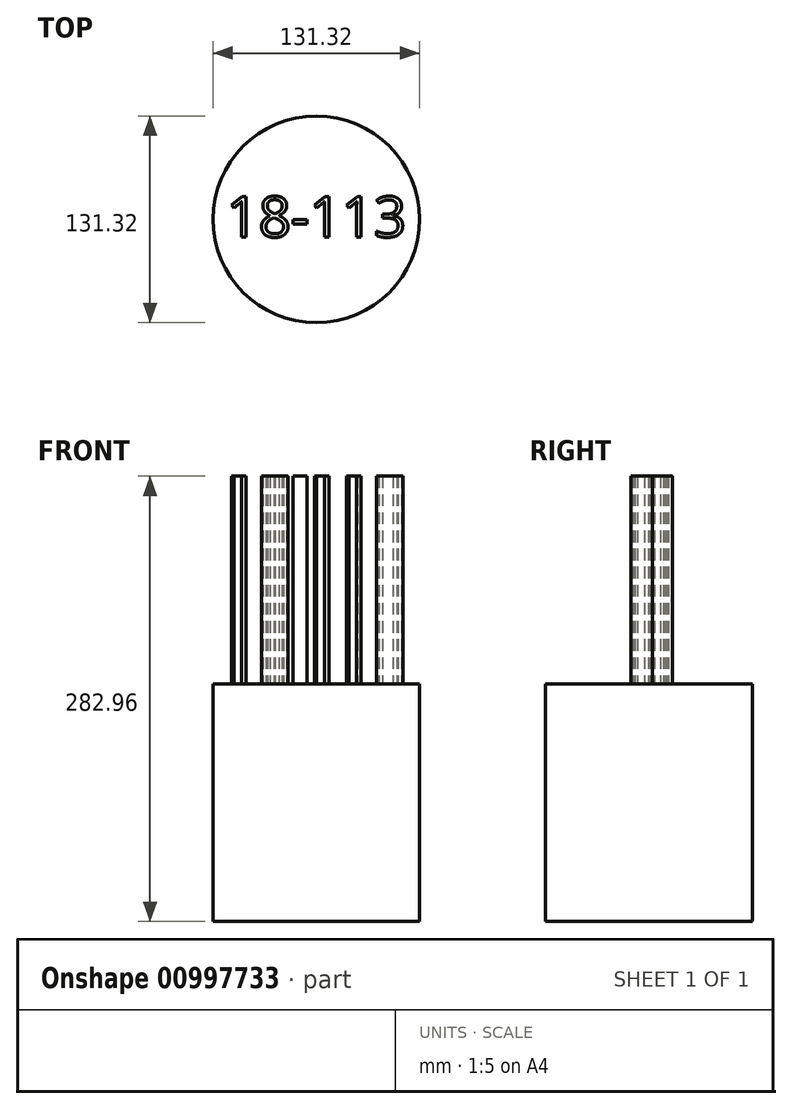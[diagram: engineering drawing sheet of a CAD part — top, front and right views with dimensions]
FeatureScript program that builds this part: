
annotation { "Feature Type Name" : "Feature", "Feature Type Description" : "" }
export const myFeature = defineFeature(function(context is Context, id is Id, definition is map)
    precondition{}
    {
        {
            var Q0;
            Q0=qCreatedBy(makeId("Top.planeOp"),FACE);
            var sketch = newSketch(context, id + "F0", { "sketchPlane" : qUnion([Q0])});
            skCircle(sketch, "E0", {"center": v(0, 0) * mm, "radius": 65.66 * mm});
            skSolve(sketch);
        }
        {
            var Q0;
            Q0 = qSketchRegion(id + "F0", true);
            extrude(context, id + "F1", {"entities" : qUnion([Q0]), "depth" : 150.88 * mm, "offsetDistance" : 25.4 * mm});
        }
        {
            var Q0;
            Q0=makeQuery(id+"F1.opExtrude","CAP_FACE",FACE,{"disambiguationData":[OSD([sQuery(id+"F0.wireOp",EDGE,"E0")])],"isStart":false});
            var sketch = newSketch(context, id + "F2", { "sketchPlane" : qUnion([Q0])});
            skText(sketch, "E1", { "text": "18-113", "fontName": "OpenSans-Regular.ttf"});
            const initialGuessF2  = {"E1": [-0.0572, -0.01124, 1, 0, 0.02585]};
            skSetInitialGuess(sketch, initialGuessF2);
            skSolve(sketch);
        }
        {
            var Q0;
            Q0=makeQuery(id+"F2.imprint","IMPRINT",FACE,{"disambiguationData":[TD([[makeQuery(id+"F2.imprint","IMPRINT",EDGE,{"derivedFrom":sQuery(id+"F2.wireOp",EDGE,"E1.sketch_text.stroke-0")}),1.0]])]});
            var sketch = newSketch(context, id + "F3", { "sketchPlane" : qUnion([Q0])});
            skSolve(sketch);
        }
        {
            var Q0;
            Q0=makeQuery(id+"F3.imprint","IMPRINT",FACE,{"disambiguationData":[TD([[makeQuery(id+"F3.imprint","IMPRINT",EDGE,{"derivedFrom":makeQuery(id+"F2.imprint","IMPRINT",EDGE,{"derivedFrom":sQuery(id+"F2.wireOp",EDGE,"E1.sketch_text.stroke-9")})}),-1.0]])]});
            var Q1;
            Q1 = qSketchRegion(id + "F2", true);
            extrude(context, id + "F4", {"entities" : qUnion([Q0, Q1]), "operationType" : NewBodyOperationType.ADD, "depth" : 132.08 * mm, "offsetDistance" : 25.4 * mm});
        }
    });
